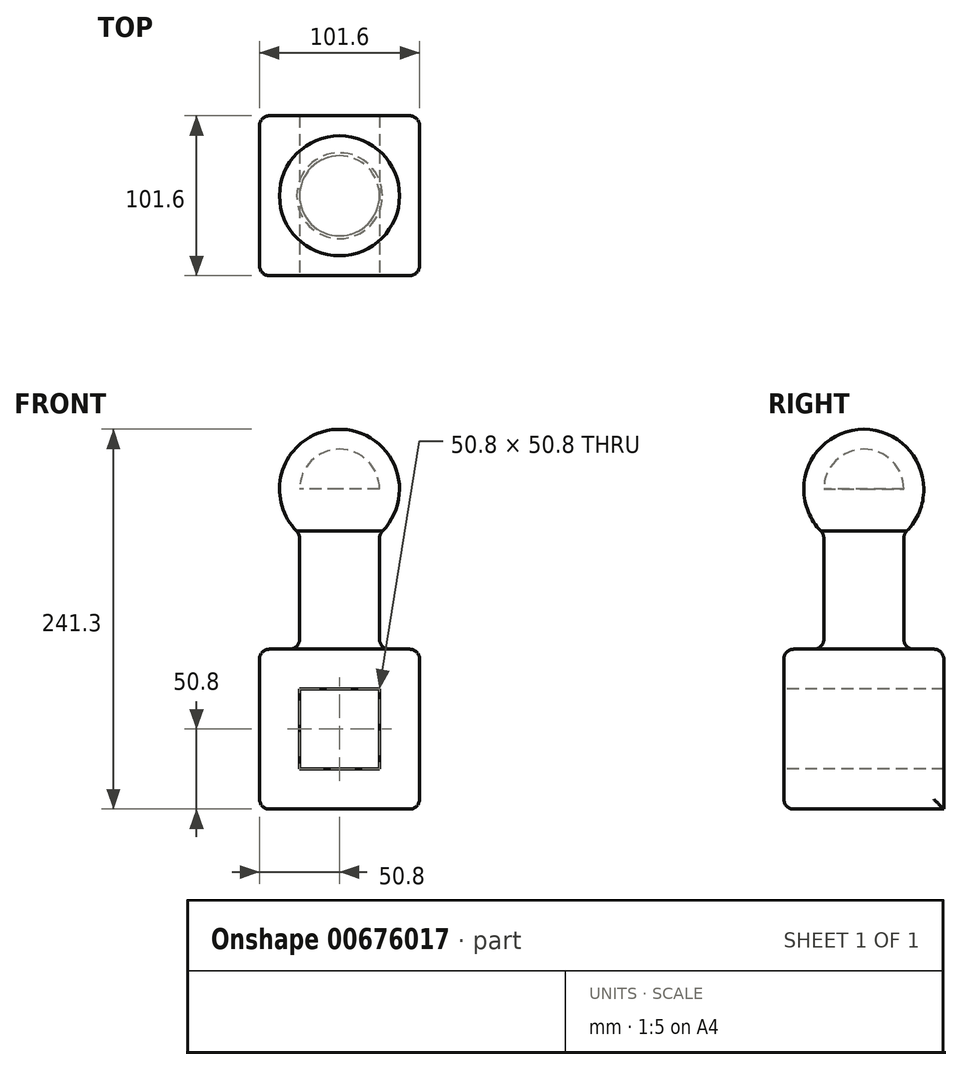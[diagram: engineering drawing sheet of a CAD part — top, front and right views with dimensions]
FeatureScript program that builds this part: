
annotation { "Feature Type Name" : "Feature", "Feature Type Description" : "" }
export const myFeature = defineFeature(function(context is Context, id is Id, definition is map)
    precondition{}
    {
        {
            var Q0;
            Q0=qCreatedBy(makeId("Top.planeOp"),FACE);
            var sketch = newSketch(context, id + "F0", { "sketchPlane" : qUnion([Q0])});
            skLineSegment(sketch, "E0.bottom", {"start": v(50.8, 50.8) * mm, "end": v(-50.8, 50.8) * mm});
            skLineSegment(sketch, "E0.top", {"start": v(50.8, -50.8) * mm, "end": v(-50.8, -50.8) * mm});
            skLineSegment(sketch, "E0.left", {"start": v(50.8, 50.8) * mm, "end": v(50.8, -50.8) * mm});
            skLineSegment(sketch, "E0.right", {"start": v(-50.8, 50.8) * mm, "end": v(-50.8, -50.8) * mm});
            skPoint(sketch, "E0.middle", {"position": v(0, 0) * mm});
            skSolve(sketch);
        }
        {
            var Q0;
            Q0 = qSketchRegion(id + "F0", true);
            extrude(context, id + "F1", {"entities" : qUnion([Q0]), "depth" : 101.6 * mm, "offsetDistance" : 25.4 * mm});
        }
        {
            var Q0;
            Q0=makeQuery(id+"F1.opExtrude","CAP_FACE",FACE,{"disambiguationData":[OSD([sQuery(id+"F0.wireOp",EDGE,"E0.bottom"),sQuery(id+"F0.wireOp",EDGE,"E0.top"),sQuery(id+"F0.wireOp",EDGE,"E0.left"),sQuery(id+"F0.wireOp",EDGE,"E0.right")])],"isStart":false});
            var sketch = newSketch(context, id + "F2", { "sketchPlane" : qUnion([Q0])});
            skCircle(sketch, "E1", {"center": v(0, 0) * mm, "radius": 25.4 * mm});
            skSolve(sketch);
        }
        {
            var Q0;
            Q0 = qSketchRegion(id + "F2", true);
            extrude(context, id + "F3", {"entities" : qUnion([Q0]), "operationType" : NewBodyOperationType.ADD, "depth" : 101.6 * mm, "offsetDistance" : 25.4 * mm});
        }
        {
            var Q0;
            Q0=makeQuery(id+"F3.opExtrude","CAP_FACE",FACE,{"disambiguationData":[OSD([sQuery(id+"F2.wireOp",EDGE,"E1")])],"isStart":false});
            var sketch = newSketch(context, id + "F4", { "sketchPlane" : qUnion([Q0])});
            skArc(sketch, "E2", {"start": v(0, -38.1) * mm, "mid": v(38.1, 0) * mm, "end": v(0, 38.1) * mm});
            skLineSegment(sketch, "E3", {"start": v(0, 0) * mm, "end": v(0, 38.1) * mm});
            skLineSegment(sketch, "E4", {"start": v(0, 38.1) * mm, "end": v(0, 0) * mm});
            skLineSegment(sketch, "E5", {"start": v(0, -38.1) * mm, "end": v(0, 0) * mm});
            skSolve(sketch);
        }
        {
            var Q0;
            {var subQ0=sQuery(id+"F4.wireOp",EDGE,"E2");Q0=makeQuery(id+"F4.imprint","IMPRINT",FACE,{"disambiguationData":[TD([[makeQuery(id+"F4.imprint","IMPRINT",EDGE,{"derivedFrom":subQ0}),1.0]])]});}
            var Q1;
            {var subQ0=sQuery(id+"F4.wireOp",EDGE,"E5");var subQ1=sQuery(id+"F4.wireOp",EDGE,"E4");var subQ2=makeQuery(id+"F4.imprint","INTERSECT",VERTEX,{"derivedFrom":[subQ1,subQ0]});Q1=makeQuery(id+"F4.imprint","IMPRINT",FACE,{"disambiguationData":[TD([[makeQuery(id+"F4.imprint","IMPRINT",EDGE,{"disambiguationData":[TD([[subQ2,1.0]])],"derivedFrom":subQ1}),1.0]])]});}
            var Q2;
            Q2=sQuery(id+"F4.wireOp",EDGE,"E5");
            revolve(context, id + "F5", {"operationType" : NewBodyOperationType.ADD, "entities" : qUnion([Q0, Q1]), "axis" : qUnion([Q2]), "revolveType" : RevolveType.FULL});
        }
        {
            var Q0;
            Q0=makeQuery(id+"F1.opExtrude","SWEPT_FACE",FACE,{"disambiguationData":[OSD([sQuery(id+"F0.wireOp",EDGE,"E0.top")])]});
            var sketch = newSketch(context, id + "F6", { "sketchPlane" : qUnion([Q0])});
            skLineSegment(sketch, "E6.bottom", {"start": v(25.4, 76.2) * mm, "end": v(-25.4, 76.2) * mm});
            skLineSegment(sketch, "E6.top", {"start": v(25.4, 25.4) * mm, "end": v(-25.4, 25.4) * mm});
            skLineSegment(sketch, "E6.left", {"start": v(25.4, 76.2) * mm, "end": v(25.4, 25.4) * mm});
            skLineSegment(sketch, "E6.right", {"start": v(-25.4, 76.2) * mm, "end": v(-25.4, 25.4) * mm});
            skPoint(sketch, "E6.middle", {"position": v(0, 50.8) * mm});
            skPoint(sketch, "E6.middle.positionSnap0", {"position": v(50.8, 50.8) * mm});
            skPoint(sketch, "E6.centerSnap0", {"position": v(50.8, 50.8) * mm});
            skSolve(sketch);
        }
        {
            var Q0;
            Q0=makeQuery(id+"F6.imprint","IMPRINT",FACE,{"disambiguationData":[TD([[makeQuery(id+"F6.imprint","IMPRINT",EDGE,{"derivedFrom":sQuery(id+"F6.wireOp",EDGE,"E6.bottom")}),1.0]])]});
            extrude(context, id + "F7", {"entities" : qUnion([Q0]), "operationType" : NewBodyOperationType.REMOVE, "oppositeDirection" : true, "depth" : 101.6 * mm, "offsetDistance" : 25.4 * mm});
        }
        {
            var Q0;
            Q0=makeQuery(id+"F1.opExtrude","CAP_EDGE",EDGE,{"disambiguationData":[OSD([sQuery(id+"F0.wireOp",EDGE,"E0.right")])],"isStart":false});
            var Q1;
            Q1=makeQuery(id+"F1.opExtrude","CAP_EDGE",EDGE,{"disambiguationData":[OSD([sQuery(id+"F0.wireOp",EDGE,"E0.top")])],"isStart":false});
            var Q2;
            Q2=makeQuery(id+"F1.opExtrude","CAP_EDGE",EDGE,{"disambiguationData":[OSD([sQuery(id+"F0.wireOp",EDGE,"E0.left")])],"isStart":false});
            var Q3;
            Q3=makeQuery(id+"F1.opExtrude","CAP_EDGE",EDGE,{"disambiguationData":[OSD([sQuery(id+"F0.wireOp",EDGE,"E0.bottom")])],"isStart":false});
            var Q4;
            Q4=makeQuery(id+"F1.opExtrude","SWEPT_EDGE",EDGE,{"disambiguationData":[OSD([sQuery(id+"F0.wireOp",EDGE,"E0.bottom"),sQuery(id+"F0.wireOp",EDGE,"E0.left")])]});
            var Q5;
            Q5=makeQuery(id+"F1.opExtrude","SWEPT_EDGE",EDGE,{"disambiguationData":[OSD([sQuery(id+"F0.wireOp",EDGE,"E0.top"),sQuery(id+"F0.wireOp",EDGE,"E0.left")])]});
            var Q6;
            Q6=makeQuery(id+"F1.opExtrude","CAP_EDGE",EDGE,{"disambiguationData":[OSD([sQuery(id+"F0.wireOp",EDGE,"E0.left")])],"isStart":true});
            var Q7;
            Q7=makeQuery(id+"F1.opExtrude","CAP_EDGE",EDGE,{"disambiguationData":[OSD([sQuery(id+"F0.wireOp",EDGE,"E0.top")])],"isStart":true});
            var Q8;
            Q8=makeQuery(id+"F1.opExtrude","SWEPT_EDGE",EDGE,{"disambiguationData":[OSD([sQuery(id+"F0.wireOp",EDGE,"E0.top"),sQuery(id+"F0.wireOp",EDGE,"E0.right")])]});
            var Q9;
            Q9=makeQuery(id+"F1.opExtrude","SWEPT_EDGE",EDGE,{"disambiguationData":[OSD([sQuery(id+"F0.wireOp",EDGE,"E0.bottom"),sQuery(id+"F0.wireOp",EDGE,"E0.right")])]});
            var Q10;
            Q10=makeQuery(id+"F1.opExtrude","CAP_EDGE",EDGE,{"disambiguationData":[OSD([sQuery(id+"F0.wireOp",EDGE,"E0.right")])],"isStart":true});
            var Q11;
            Q11=makeQuery(id+"F3.opExtrude","SWEPT_FACE",FACE,{"disambiguationData":[OSD([sQuery(id+"F2.wireOp",EDGE,"E1")])]});
            fillet(context, id + "F8", {"entities" : qUnion([Q0, Q1, Q2, Q3, Q4, Q5, Q6, Q7, Q8, Q9, Q10, Q11]), "radius" : 6.35 * mm, "tangentPropagation" : true, "allowEdgeOverflow" : false});
        }
    });
